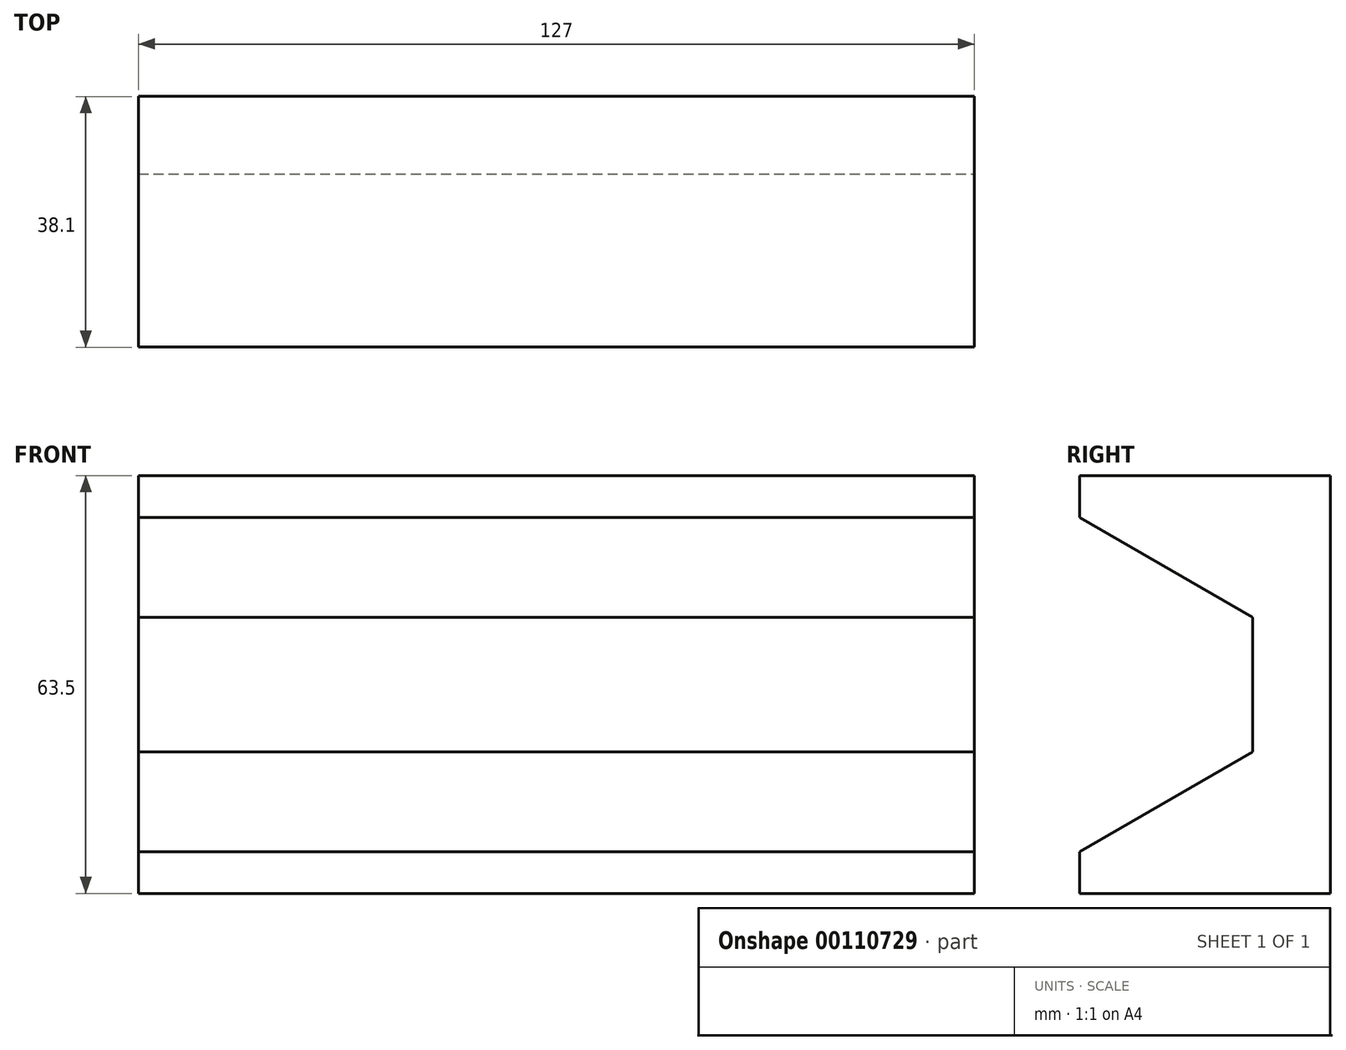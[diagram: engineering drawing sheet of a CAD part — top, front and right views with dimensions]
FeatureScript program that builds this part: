
annotation { "Feature Type Name" : "Feature", "Feature Type Description" : "" }
export const myFeature = defineFeature(function(context is Context, id is Id, definition is map)
    precondition{}
    {
        {
            var Q0;
            Q0=qCreatedBy(makeId("Right.planeOp"),FACE);
            var sketch = newSketch(context, id + "F0", { "sketchPlane" : qUnion([Q0])});
            skLineSegment(sketch, "E0", {"start": v(-25.66, -10) * mm, "end": v(-25.66, -16.35) * mm});
            skLineSegment(sketch, "E1", {"start": v(-25.66, -16.35) * mm, "end": v(12.44, -16.35) * mm});
            skLineSegment(sketch, "E2", {"start": v(12.44, -16.35) * mm, "end": v(12.44, 47.15) * mm});
            skLineSegment(sketch, "E3", {"start": v(12.44, 47.15) * mm, "end": v(-25.66, 47.15) * mm});
            skPoint(sketch, "E3.endSnap0", {"position": v(-25.66, -13.18) * mm});
            skLineSegment(sketch, "E4", {"start": v(-25.66, 47.15) * mm, "end": v(-25.66, 40.8) * mm});
            skLineSegment(sketch, "E5", {"start": v(-25.66, 40.8) * mm, "end": v(0.64, 25.61) * mm});
            skLineSegment(sketch, "E6", {"start": v(-25.66, -10) * mm, "end": v(0.64, 5.18) * mm});
            skLineSegment(sketch, "E7", {"start": v(0.64, 5.18) * mm, "end": v(0.64, 25.61) * mm});
            skSolve(sketch);
        }
        {
            var Q0;
            Q0=makeQuery(id+"F0.imprint","IMPRINT",FACE,{"disambiguationData":[TD([[makeQuery(id+"F0.imprint","IMPRINT",EDGE,{"derivedFrom":sQuery(id+"F0.wireOp",EDGE,"E0")}),1.0]])]});
            extrude(context, id + "F1", {"entities" : qUnion([Q0]), "oppositeDirection" : true, "depth" : 127 * mm});
        }
    });
